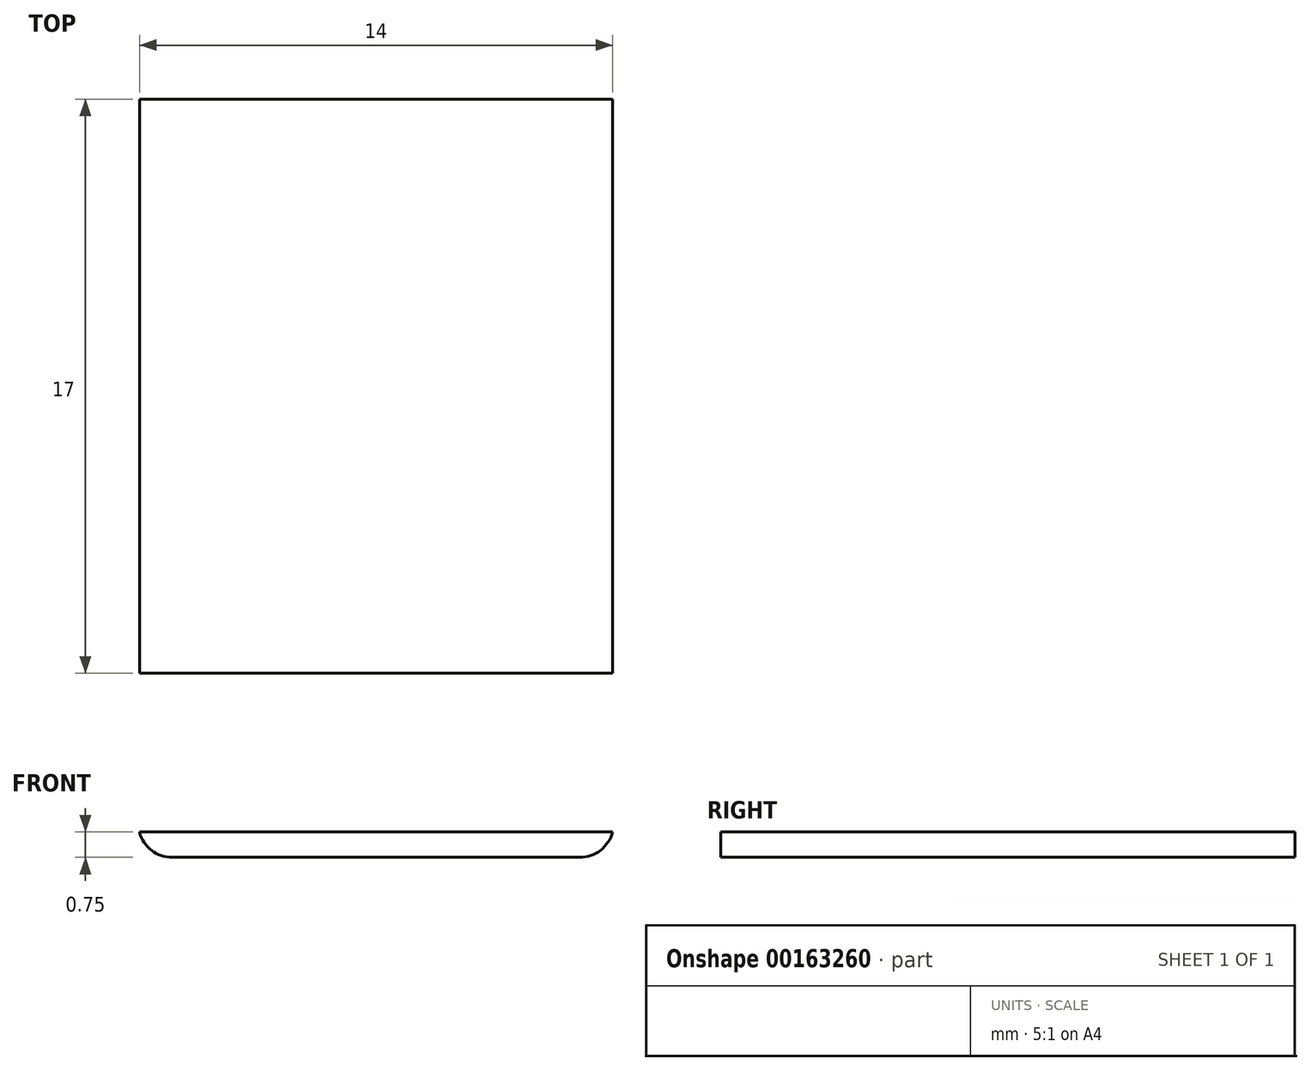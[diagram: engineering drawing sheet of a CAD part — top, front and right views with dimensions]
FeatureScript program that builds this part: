
annotation { "Feature Type Name" : "Feature", "Feature Type Description" : "" }
export const myFeature = defineFeature(function(context is Context, id is Id, definition is map)
    precondition{}
    {
        {
            var Q0;
            Q0=qCreatedBy(makeId("Top.planeOp"),FACE);
            var sketch = newSketch(context, id + "F0", { "sketchPlane" : qUnion([Q0])});
            skLineSegment(sketch, "E0.bottom", {"start": v(0, 0) * mm, "end": v(14, 0) * mm});
            skLineSegment(sketch, "E0.top", {"start": v(0, 17) * mm, "end": v(14, 17) * mm});
            skLineSegment(sketch, "E0.left", {"start": v(0, 0) * mm, "end": v(0, 17) * mm});
            skLineSegment(sketch, "E0.right", {"start": v(14, 0) * mm, "end": v(14, 17) * mm});
            skSolve(sketch);
        }
        {
            var Q0;
            Q0 = qSketchRegion(id + "F0", true);
            extrude(context, id + "F1", {"entities" : qUnion([Q0]), "depth" : .75 * mm});
        }
        {
            var Q0;
            Q0=makeQuery(id+"F1.opExtrude","CAP_EDGE",EDGE,{"disambiguationData":[OSD([sQuery(id+"F0.wireOp",EDGE,"E0.right")])],"isStart":true});
            var Q1;
            Q1=makeQuery(id+"F1.opExtrude","CAP_EDGE",EDGE,{"disambiguationData":[OSD([sQuery(id+"F0.wireOp",EDGE,"E0.left")])],"isStart":true});
            fillet(context, id + "F2", {"entities" : qUnion([Q0, Q1]), "radius" : 1 * mm, "tangentPropagation" : true, "allowEdgeOverflow" : false});
        }
    });
